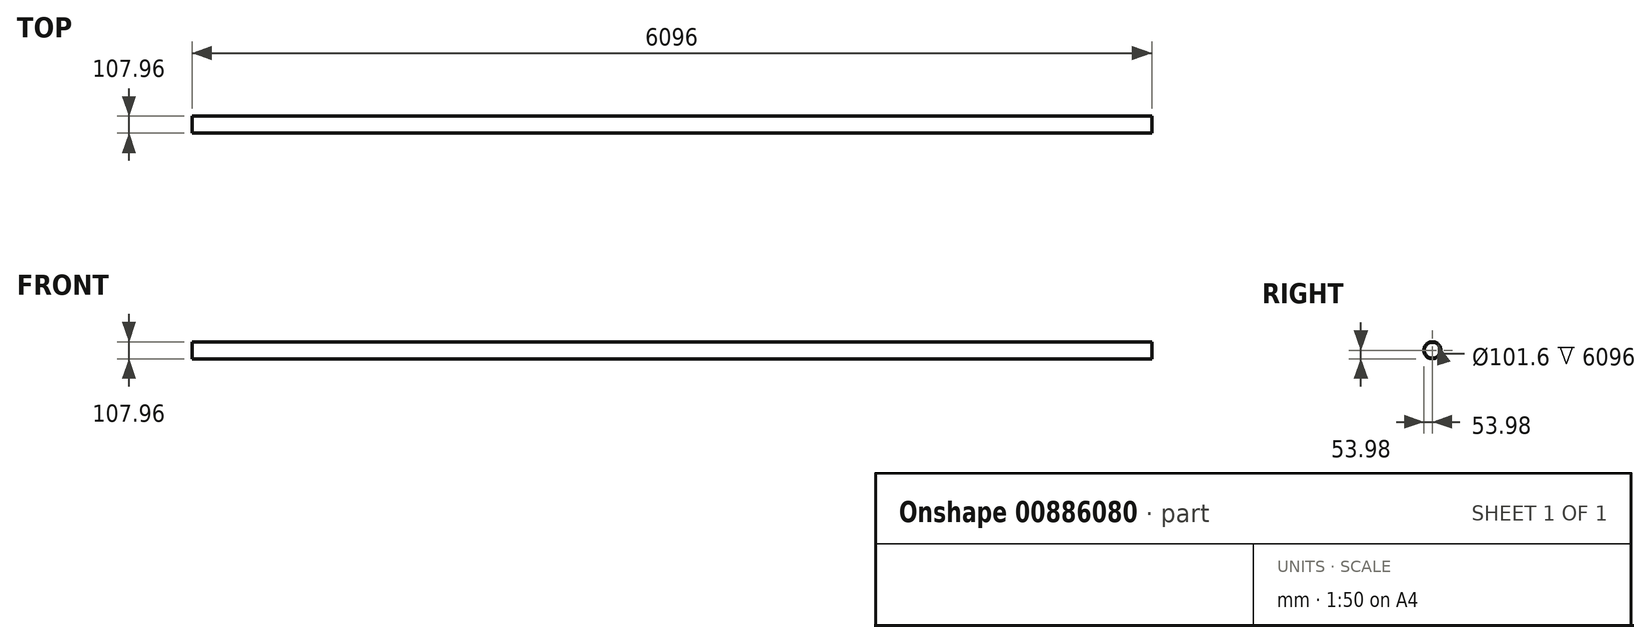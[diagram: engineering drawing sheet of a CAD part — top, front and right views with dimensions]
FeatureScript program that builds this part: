
annotation { "Feature Type Name" : "Feature", "Feature Type Description" : "" }
export const myFeature = defineFeature(function(context is Context, id is Id, definition is map)
    precondition{}
    {
        {
            var Q0;
            Q0=qCreatedBy(makeId("Right.planeOp"),FACE);
            var sketch = newSketch(context, id + "F0", { "sketchPlane" : qUnion([Q0])});
            skCircle(sketch, "E0", {"center": v(0, 0) * mm, "radius": 50.8 * mm});
            skCircle(sketch, "E1", {"center": v(0, 0) * mm, "radius": 53.98 * mm});
            skSolve(sketch);
        }
        {
            var Q0;
            Q0 = qSketchRegion(id + "F0", true);
            extrude(context, id + "F1", {"entities" : qUnion([Q0]), "depth" : 6096 * mm, "offsetDistance" : 25 * mm});
        }
    });
